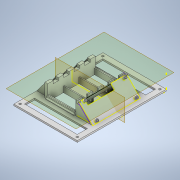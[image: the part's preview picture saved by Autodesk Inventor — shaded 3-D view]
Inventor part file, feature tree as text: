
AUTODESK INVENTOR PART (.ipt)
format: ipt  version: 2020.1 (Build 241239000, 239)  size: 667,136 bytes
history: native  units: mm
features: sketch x37, extrude x23, projected_geometry x16, chamfer x4, mirror x4, plane x3, hole x1, pattern_linear x1
ambient origin geometry x8: Origin, YZ Plane, XZ Plane, XY Plane, X Axis, Y Axis, Z Axis, Center Point
bodies: Solid1 (feature_tree)
feature tree (89):
  extrude  "Extrusion1"  Depth=168.0mm
  sketch  "Sketch2"  dims[d4=3.0mm d5=0.0mm d6=90.0mm]
  extrude  "Extrusion2"  Depth=90.0mm
  chamfer  "Chamfer1"  Distance=40.0mm
  sketch  "Sketch4"  dims[d8=20.0mm]
  extrude  "Extrusion3"  Depth=3.0mm
  sketch  "Sketch8"  dims[d10=39.0mm]
  extrude  "Extrusion5"  Depth=3.0mm
  sketch  "Sketch9"  dims[d11=39.0mm d12=40.0mm d13=0.0mm]
  sketch  "Sketch10"  dims[d14=40.0mm d15=2.0mm d16=45.0deg d17=3.0mm]
  sketch  "Sketch11"  dims[d18=3.0mm d19=3.0mm]
  extrude  "Extrusion6"  Depth=31.0mm
  extrude  "Extrusion7"  Depth=75.0mm
  extrude  "Extrusion8"  Depth=90.0mm
  sketch  "Sketch15"  dims[d26=7.5mm d27=0.0mm]
  sketch  "Sketch17"  dims[d28=3.0mm d29=0.0mm]
  sketch  "Sketch18"  dims[d30=34.0mm d31=3.0mm]
  sketch  "Sketch19"  dims[d32=300.0mm d33=0.0mm d37=5.0mm]
  extrude  "Extrusion10"  TaperAngle=0.0deg  [1 undecoded]
  extrude  "Extrusion11"  TaperAngle=0.0deg  [1 undecoded]
  extrude  "Extrusion12"  Depth=3.0mm
  extrude  "Extrusion13"  Depth=5.0mm
  extrude  "Extrusion14"  Depth=5.0mm
  hole  "Hole1"  [1 undecoded]
  extrude  "Extrusion16"  Depth=5.4185mm
  chamfer  "Chamfer2"  Distance=40.0mm
  extrude  "Extrusion17"  Depth=90.0mm
  extrude  "Extrusion18"  Depth=90.0mm
  plane  "Work Plane1"
  mirror  "Mirror1"
  extrude  "Extrusion19"  Depth=2.0mm
  sketch  "Sketch31"  dims[d78=10.0mm d79=0.0mm]
  extrude  "Extrusion20"  Depth=10.0mm TaperAngle=0.0deg
  pattern_linear  "Rectangular Pattern1"  Count1=5  [1 undecoded]
  plane  "Work Plane2"
  sketch  "Sketch36"  dims[d82=10.0mm d83=0.0mm d84=20.0mm d85=50.0mm d86=0.0mm d87=0.0mm d88=20.0mm d89=0.0mm]
  extrude  "Extrusion23"  Depth=20.0mm TaperAngle=0.0deg
  chamfer  "Chamfer4"  Distance=20.0mm
  mirror  "Mirror2"
  extrude  "Extrusion24"  Depth=6.0mm
  mirror  "Mirror3"
  extrude  "Extrusion26"  Depth=5.0mm
  extrude  "Extrusion27"  Depth=1.5mm
  extrude  "Extrusion28"  Depth=5.0mm TaperAngle=0.0deg
  sketch  "Sketch43"  dims[d114=20.0mm d115=26.613mm d116=45.0deg d117=5.0mm d118=0.0mm d119=3.0mm d120=0.0mm]
  sketch  "Sketch48"  dims[d121=5.0mm d122=0.0mm]
  plane  "Work Plane3"
  extrude  "Extrusion31"  Depth=5.0mm TaperAngle=0.0deg
  chamfer  "Chamfer6"  Distance=3.0mm
  mirror  "Mirror4"
  sketch  "Sketch1"  dims[d2=120.0mm d3=168.0mm]
  sketch  "Sketch3"  dims[d7=90.0mm]
  sketch  "Sketch5"  dims[d9=10.0mm]
  sketch  "Sketch12"  dims[d20=3.0mm d21=31.0mm]
  sketch  "Sketch13"  dims[d22=31.0mm d23=75.0mm]
  sketch  "Sketch14"  dims[d24=75.0mm d25=90.0mm]
  projected_geometry  "Projected Loop1"
  projected_geometry  "Projected Loop2"
  projected_geometry  "Projected Loop3"
  sketch  "Sketch20"  dims[d38=5.0mm d39=5.0mm]
  projected_geometry  "Projected Loop4"
  sketch  "Sketch21"  dims[d40=5.0mm d41=5.0mm d42=0.0mm]
  projected_geometry  "Projected Loop5"
  sketch  "Sketch22"  dims[d43=53.0mm d44=5.4185mm]
  sketch  "Sketch23"  dims[d45=5.418567mm]
  sketch  "Sketch24"  dims[d46=0.0mm]
  sketch  "Sketch26"  dims[d47=90.0mm d48=40.0mm d49=0.0mm]
  projected_geometry  "Projected Loop6"
  sketch  "Sketch27"  dims[d50=10.0mm d51=90.0mm]
  sketch  "Sketch28"  dims[d52=10.0mm d53=90.0mm d55=10.0mm d56=10.0mm d58=10.0mm]
  projected_geometry  "Projected Loop7"
  sketch  "Sketch29"  dims[d60=5.0mm d61=0.0mm d62=2.0mm]
  projected_geometry  "Projected Loop8"
  sketch  "Sketch30"  dims[d63=0.0mm d64=0.0mm d76=10.0mm d77=0.0mm]
  projected_geometry  "Projected Loop9"
  sketch  "Sketch32"  dims[d80=10.0mm d81=50.0mm]
  sketch  "Sketch37"  dims[d92=6.0mm]
  sketch  "Sketch38"  dims[d93=4.0mm d94=6.0mm d95=8.4mm d96=2.0mm d97=90.0deg d98=8.0mm d99=20.594885mm d100=6.0mm]
  projected_geometry  "Projected Loop14"
  sketch  "Sketch40"  dims[d101=180.0deg d102=5.0mm]
  projected_geometry  "Projected Loop16"
  sketch  "Sketch41"  dims[d103=5.0mm d104=1.5mm]
  projected_geometry  "Projected Loop17"
  sketch  "Sketch42"  dims[d105=50.0mm d107=20.0mm d108=10.0mm d110=10.0mm d112=5.0mm d113=0.0mm]
  projected_geometry  "Projected Loop18"
  projected_geometry  "Projected Loop19"
  projected_geometry  "Projected Loop20"
  sketch  "Sketch49"  dims[d123=2.0mm d124=10.543mm d125=5.0mm d126=0.0mm d127=40.0mm d129=29.333333mm d138=3.0mm d139=4.0mm d140=0.0mm d144=2.0mm d145=2.0mm d146=45.0deg d147=2.0mm d148=0.0mm d157=13.0mm d158=2.0mm d159=0.0mm d160=0.0mm d167=10.0mm d168=10.0mm d169=0.0mm d170=0.05mm d171=0.25mm d172=41.581mm d173=0.0mm d184=1.5mm d185=2.0mm d186=4.0mm d187=0.0mm d188=1.5mm d189=2.0mm d190=45.0deg d73=0.5mm d74=0.872665mm d75=0.5mm d106=0.872665mm d153=0.5mm d154=0.872665mm d155=0.5mm d156=0.872665mm d176=0.872665mm d177=0.872665mm]
  projected_geometry  "Projected Loop21"
note: 4 required parameter values undecoded (feature->parameter linkage not recoverable at this tier; creation-order binding heuristic only, values carry confidence <= 0.55)
